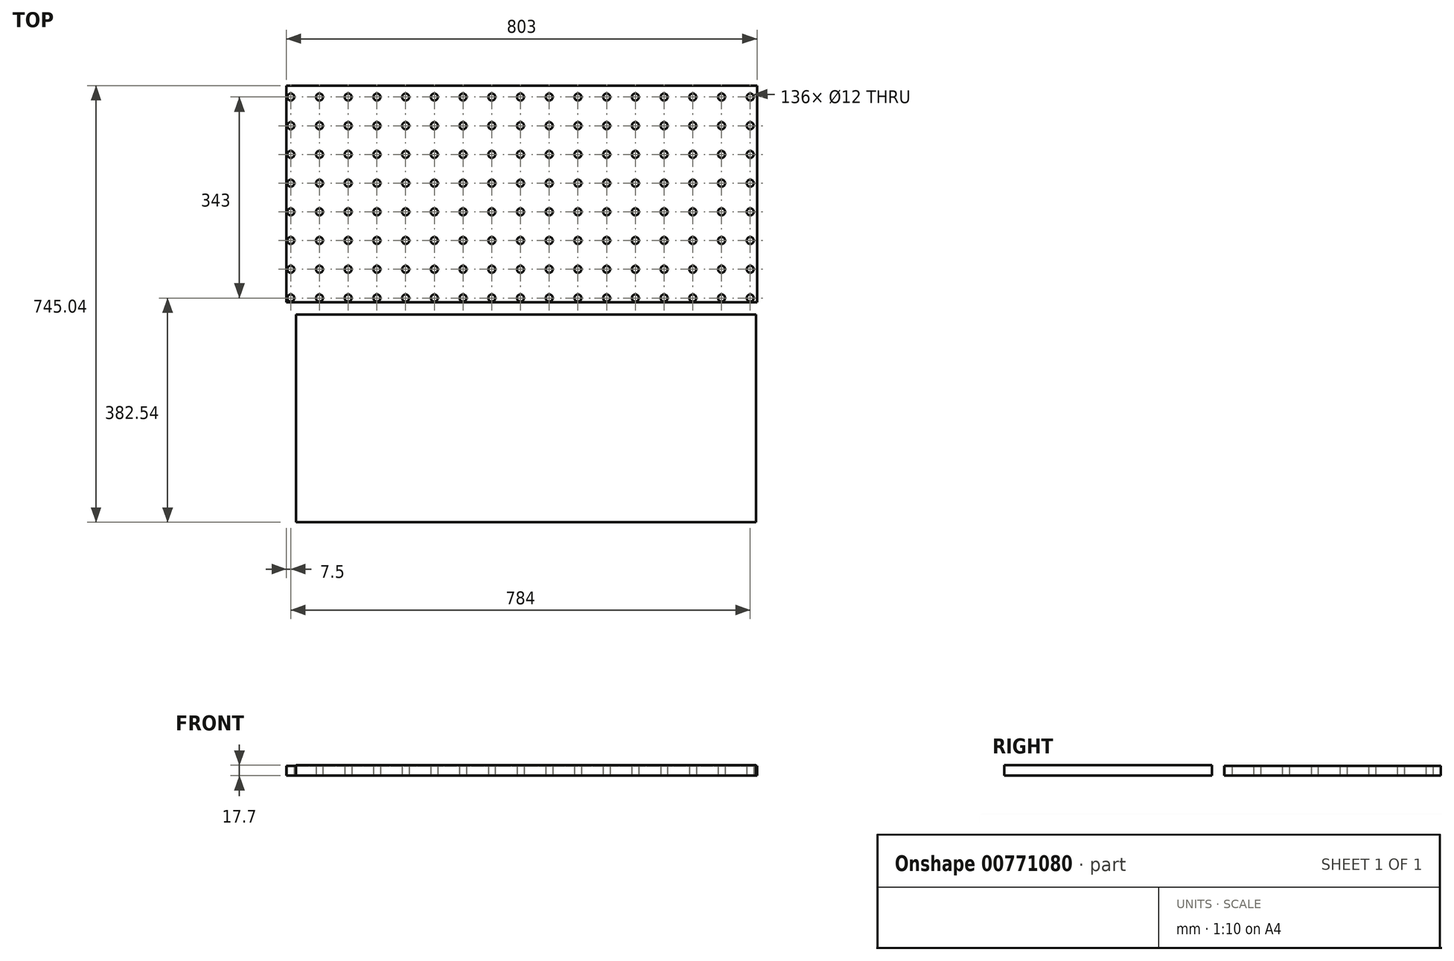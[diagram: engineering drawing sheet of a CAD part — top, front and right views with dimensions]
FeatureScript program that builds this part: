
annotation { "Feature Type Name" : "Feature", "Feature Type Description" : "" }
export const myFeature = defineFeature(function(context is Context, id is Id, definition is map)
    precondition{}
    {
        {
            var Q0;
            Q0=qCreatedBy(makeId("Top.planeOp"),FACE);
            var sketch = newSketch(context, id + "F0", { "sketchPlane" : qUnion([Q0])});
            skLineSegment(sketch, "E0.bottom", {"start": v(-401.5, 185) * mm, "end": v(401.5, 185) * mm});
            skLineSegment(sketch, "E0.top", {"start": v(-401.5, -185) * mm, "end": v(401.5, -185) * mm});
            skLineSegment(sketch, "E0.left", {"start": v(-401.5, 185) * mm, "end": v(-401.5, -185) * mm});
            skLineSegment(sketch, "E0.right", {"start": v(401.5, 185) * mm, "end": v(401.5, -185) * mm});
            skCircle(sketch, "E1", {"center": v(-394, -177.5) * mm, "radius": 6 * mm});
            skCircle(sketch, "E2.0.1.0", {"center": v(-394, -128.5) * mm, "radius": 6 * mm});
            skCircle(sketch, "E2.0.2.0", {"center": v(-394, -79.5) * mm, "radius": 6 * mm});
            skCircle(sketch, "E2.0.3.0", {"center": v(-394, -30.5) * mm, "radius": 6 * mm});
            skCircle(sketch, "E2.0.4.0", {"center": v(-394, 18.5) * mm, "radius": 6 * mm});
            skCircle(sketch, "E2.0.5.0", {"center": v(-394, 67.5) * mm, "radius": 6 * mm});
            skCircle(sketch, "E2.0.6.0", {"center": v(-394, 116.5) * mm, "radius": 6 * mm});
            skCircle(sketch, "E2.0.7.0", {"center": v(-394, 165.5) * mm, "radius": 6 * mm});
            skCircle(sketch, "E2.1.0.0", {"center": v(-345, -177.5) * mm, "radius": 6 * mm});
            skCircle(sketch, "E2.1.1.0", {"center": v(-345, -128.5) * mm, "radius": 6 * mm});
            skCircle(sketch, "E2.1.2.0", {"center": v(-345, -79.5) * mm, "radius": 6 * mm});
            skCircle(sketch, "E2.1.3.0", {"center": v(-345, -30.5) * mm, "radius": 6 * mm});
            skCircle(sketch, "E2.1.4.0", {"center": v(-345, 18.5) * mm, "radius": 6 * mm});
            skCircle(sketch, "E2.1.5.0", {"center": v(-345, 67.5) * mm, "radius": 6 * mm});
            skCircle(sketch, "E2.1.6.0", {"center": v(-345, 116.5) * mm, "radius": 6 * mm});
            skCircle(sketch, "E2.1.7.0", {"center": v(-345, 165.5) * mm, "radius": 6 * mm});
            skCircle(sketch, "E2.2.0.0", {"center": v(-296, -177.5) * mm, "radius": 6 * mm});
            skCircle(sketch, "E2.2.1.0", {"center": v(-296, -128.5) * mm, "radius": 6 * mm});
            skCircle(sketch, "E2.2.2.0", {"center": v(-296, -79.5) * mm, "radius": 6 * mm});
            skCircle(sketch, "E2.2.3.0", {"center": v(-296, -30.5) * mm, "radius": 6 * mm});
            skCircle(sketch, "E2.2.4.0", {"center": v(-296, 18.5) * mm, "radius": 6 * mm});
            skCircle(sketch, "E2.2.5.0", {"center": v(-296, 67.5) * mm, "radius": 6 * mm});
            skCircle(sketch, "E2.2.6.0", {"center": v(-296, 116.5) * mm, "radius": 6 * mm});
            skCircle(sketch, "E2.2.7.0", {"center": v(-296, 165.5) * mm, "radius": 6 * mm});
            skCircle(sketch, "E2.3.0.0", {"center": v(-247, -177.5) * mm, "radius": 6 * mm});
            skCircle(sketch, "E2.3.1.0", {"center": v(-247, -128.5) * mm, "radius": 6 * mm});
            skCircle(sketch, "E2.3.2.0", {"center": v(-247, -79.5) * mm, "radius": 6 * mm});
            skCircle(sketch, "E2.3.3.0", {"center": v(-247, -30.5) * mm, "radius": 6 * mm});
            skCircle(sketch, "E2.3.4.0", {"center": v(-247, 18.5) * mm, "radius": 6 * mm});
            skCircle(sketch, "E2.3.5.0", {"center": v(-247, 67.5) * mm, "radius": 6 * mm});
            skCircle(sketch, "E2.3.6.0", {"center": v(-247, 116.5) * mm, "radius": 6 * mm});
            skCircle(sketch, "E2.3.7.0", {"center": v(-247, 165.5) * mm, "radius": 6 * mm});
            skCircle(sketch, "E2.4.0.0", {"center": v(-198, -177.5) * mm, "radius": 6 * mm});
            skCircle(sketch, "E2.4.1.0", {"center": v(-198, -128.5) * mm, "radius": 6 * mm});
            skCircle(sketch, "E2.4.2.0", {"center": v(-198, -79.5) * mm, "radius": 6 * mm});
            skCircle(sketch, "E2.4.3.0", {"center": v(-198, -30.5) * mm, "radius": 6 * mm});
            skCircle(sketch, "E2.4.4.0", {"center": v(-198, 18.5) * mm, "radius": 6 * mm});
            skCircle(sketch, "E2.4.5.0", {"center": v(-198, 67.5) * mm, "radius": 6 * mm});
            skCircle(sketch, "E2.4.6.0", {"center": v(-198, 116.5) * mm, "radius": 6 * mm});
            skCircle(sketch, "E2.4.7.0", {"center": v(-198, 165.5) * mm, "radius": 6 * mm});
            skCircle(sketch, "E2.5.0.0", {"center": v(-149, -177.5) * mm, "radius": 6 * mm});
            skCircle(sketch, "E2.5.1.0", {"center": v(-149, -128.5) * mm, "radius": 6 * mm});
            skCircle(sketch, "E2.5.2.0", {"center": v(-149, -79.5) * mm, "radius": 6 * mm});
            skCircle(sketch, "E2.5.3.0", {"center": v(-149, -30.5) * mm, "radius": 6 * mm});
            skCircle(sketch, "E2.5.4.0", {"center": v(-149, 18.5) * mm, "radius": 6 * mm});
            skCircle(sketch, "E2.5.5.0", {"center": v(-149, 67.5) * mm, "radius": 6 * mm});
            skCircle(sketch, "E2.5.6.0", {"center": v(-149, 116.5) * mm, "radius": 6 * mm});
            skCircle(sketch, "E2.5.7.0", {"center": v(-149, 165.5) * mm, "radius": 6 * mm});
            skCircle(sketch, "E2.6.0.0", {"center": v(-100, -177.5) * mm, "radius": 6 * mm});
            skCircle(sketch, "E2.6.1.0", {"center": v(-100, -128.5) * mm, "radius": 6 * mm});
            skCircle(sketch, "E2.6.2.0", {"center": v(-100, -79.5) * mm, "radius": 6 * mm});
            skCircle(sketch, "E2.6.3.0", {"center": v(-100, -30.5) * mm, "radius": 6 * mm});
            skCircle(sketch, "E2.6.4.0", {"center": v(-100, 18.5) * mm, "radius": 6 * mm});
            skCircle(sketch, "E2.6.5.0", {"center": v(-100, 67.5) * mm, "radius": 6 * mm});
            skCircle(sketch, "E2.6.6.0", {"center": v(-100, 116.5) * mm, "radius": 6 * mm});
            skCircle(sketch, "E2.6.7.0", {"center": v(-100, 165.5) * mm, "radius": 6 * mm});
            skCircle(sketch, "E2.7.0.0", {"center": v(-51, -177.5) * mm, "radius": 6 * mm});
            skCircle(sketch, "E2.7.1.0", {"center": v(-51, -128.5) * mm, "radius": 6 * mm});
            skCircle(sketch, "E2.7.2.0", {"center": v(-51, -79.5) * mm, "radius": 6 * mm});
            skCircle(sketch, "E2.7.3.0", {"center": v(-51, -30.5) * mm, "radius": 6 * mm});
            skCircle(sketch, "E2.7.4.0", {"center": v(-51, 18.5) * mm, "radius": 6 * mm});
            skCircle(sketch, "E2.7.5.0", {"center": v(-51, 67.5) * mm, "radius": 6 * mm});
            skCircle(sketch, "E2.7.6.0", {"center": v(-51, 116.5) * mm, "radius": 6 * mm});
            skCircle(sketch, "E2.7.7.0", {"center": v(-51, 165.5) * mm, "radius": 6 * mm});
            skCircle(sketch, "E2.8.0.0", {"center": v(-2, -177.5) * mm, "radius": 6 * mm});
            skCircle(sketch, "E2.8.1.0", {"center": v(-2, -128.5) * mm, "radius": 6 * mm});
            skCircle(sketch, "E2.8.2.0", {"center": v(-2, -79.5) * mm, "radius": 6 * mm});
            skCircle(sketch, "E2.8.3.0", {"center": v(-2, -30.5) * mm, "radius": 6 * mm});
            skCircle(sketch, "E2.8.4.0", {"center": v(-2, 18.5) * mm, "radius": 6 * mm});
            skCircle(sketch, "E2.8.5.0", {"center": v(-2, 67.5) * mm, "radius": 6 * mm});
            skCircle(sketch, "E2.8.6.0", {"center": v(-2, 116.5) * mm, "radius": 6 * mm});
            skCircle(sketch, "E2.8.7.0", {"center": v(-2, 165.5) * mm, "radius": 6 * mm});
            skCircle(sketch, "E2.9.0.0", {"center": v(47, -177.5) * mm, "radius": 6 * mm});
            skCircle(sketch, "E2.9.1.0", {"center": v(47, -128.5) * mm, "radius": 6 * mm});
            skCircle(sketch, "E2.9.2.0", {"center": v(47, -79.5) * mm, "radius": 6 * mm});
            skCircle(sketch, "E2.9.3.0", {"center": v(47, -30.5) * mm, "radius": 6 * mm});
            skCircle(sketch, "E2.9.4.0", {"center": v(47, 18.5) * mm, "radius": 6 * mm});
            skCircle(sketch, "E2.9.5.0", {"center": v(47, 67.5) * mm, "radius": 6 * mm});
            skCircle(sketch, "E2.9.6.0", {"center": v(47, 116.5) * mm, "radius": 6 * mm});
            skCircle(sketch, "E2.9.7.0", {"center": v(47, 165.5) * mm, "radius": 6 * mm});
            skCircle(sketch, "E2.10.0.0", {"center": v(96, -177.5) * mm, "radius": 6 * mm});
            skCircle(sketch, "E2.10.1.0", {"center": v(96, -128.5) * mm, "radius": 6 * mm});
            skCircle(sketch, "E2.10.2.0", {"center": v(96, -79.5) * mm, "radius": 6 * mm});
            skCircle(sketch, "E2.10.3.0", {"center": v(96, -30.5) * mm, "radius": 6 * mm});
            skCircle(sketch, "E2.10.4.0", {"center": v(96, 18.5) * mm, "radius": 6 * mm});
            skCircle(sketch, "E2.10.5.0", {"center": v(96, 67.5) * mm, "radius": 6 * mm});
            skCircle(sketch, "E2.10.6.0", {"center": v(96, 116.5) * mm, "radius": 6 * mm});
            skCircle(sketch, "E2.10.7.0", {"center": v(96, 165.5) * mm, "radius": 6 * mm});
            skCircle(sketch, "E2.11.0.0", {"center": v(145, -177.5) * mm, "radius": 6 * mm});
            skCircle(sketch, "E2.11.1.0", {"center": v(145, -128.5) * mm, "radius": 6 * mm});
            skCircle(sketch, "E2.11.2.0", {"center": v(145, -79.5) * mm, "radius": 6 * mm});
            skCircle(sketch, "E2.11.3.0", {"center": v(145, -30.5) * mm, "radius": 6 * mm});
            skCircle(sketch, "E2.11.4.0", {"center": v(145, 18.5) * mm, "radius": 6 * mm});
            skCircle(sketch, "E2.11.5.0", {"center": v(145, 67.5) * mm, "radius": 6 * mm});
            skCircle(sketch, "E2.11.6.0", {"center": v(145, 116.5) * mm, "radius": 6 * mm});
            skCircle(sketch, "E2.11.7.0", {"center": v(145, 165.5) * mm, "radius": 6 * mm});
            skCircle(sketch, "E2.12.0.0", {"center": v(194, -177.5) * mm, "radius": 6 * mm});
            skCircle(sketch, "E2.12.1.0", {"center": v(194, -128.5) * mm, "radius": 6 * mm});
            skCircle(sketch, "E2.12.2.0", {"center": v(194, -79.5) * mm, "radius": 6 * mm});
            skCircle(sketch, "E2.12.3.0", {"center": v(194, -30.5) * mm, "radius": 6 * mm});
            skCircle(sketch, "E2.12.4.0", {"center": v(194, 18.5) * mm, "radius": 6 * mm});
            skCircle(sketch, "E2.12.5.0", {"center": v(194, 67.5) * mm, "radius": 6 * mm});
            skCircle(sketch, "E2.12.6.0", {"center": v(194, 116.5) * mm, "radius": 6 * mm});
            skCircle(sketch, "E2.12.7.0", {"center": v(194, 165.5) * mm, "radius": 6 * mm});
            skCircle(sketch, "E2.13.0.0", {"center": v(243, -177.5) * mm, "radius": 6 * mm});
            skCircle(sketch, "E2.13.1.0", {"center": v(243, -128.5) * mm, "radius": 6 * mm});
            skCircle(sketch, "E2.13.2.0", {"center": v(243, -79.5) * mm, "radius": 6 * mm});
            skCircle(sketch, "E2.13.3.0", {"center": v(243, -30.5) * mm, "radius": 6 * mm});
            skCircle(sketch, "E2.13.4.0", {"center": v(243, 18.5) * mm, "radius": 6 * mm});
            skCircle(sketch, "E2.13.5.0", {"center": v(243, 67.5) * mm, "radius": 6 * mm});
            skCircle(sketch, "E2.13.6.0", {"center": v(243, 116.5) * mm, "radius": 6 * mm});
            skCircle(sketch, "E2.13.7.0", {"center": v(243, 165.5) * mm, "radius": 6 * mm});
            skCircle(sketch, "E2.14.0.0", {"center": v(292, -177.5) * mm, "radius": 6 * mm});
            skCircle(sketch, "E2.14.1.0", {"center": v(292, -128.5) * mm, "radius": 6 * mm});
            skCircle(sketch, "E2.14.2.0", {"center": v(292, -79.5) * mm, "radius": 6 * mm});
            skCircle(sketch, "E2.14.3.0", {"center": v(292, -30.5) * mm, "radius": 6 * mm});
            skCircle(sketch, "E2.14.4.0", {"center": v(292, 18.5) * mm, "radius": 6 * mm});
            skCircle(sketch, "E2.14.5.0", {"center": v(292, 67.5) * mm, "radius": 6 * mm});
            skCircle(sketch, "E2.14.6.0", {"center": v(292, 116.5) * mm, "radius": 6 * mm});
            skCircle(sketch, "E2.14.7.0", {"center": v(292, 165.5) * mm, "radius": 6 * mm});
            skCircle(sketch, "E2.15.0.0", {"center": v(341, -177.5) * mm, "radius": 6 * mm});
            skCircle(sketch, "E2.15.1.0", {"center": v(341, -128.5) * mm, "radius": 6 * mm});
            skCircle(sketch, "E2.15.2.0", {"center": v(341, -79.5) * mm, "radius": 6 * mm});
            skCircle(sketch, "E2.15.3.0", {"center": v(341, -30.5) * mm, "radius": 6 * mm});
            skCircle(sketch, "E2.15.4.0", {"center": v(341, 18.5) * mm, "radius": 6 * mm});
            skCircle(sketch, "E2.15.5.0", {"center": v(341, 67.5) * mm, "radius": 6 * mm});
            skCircle(sketch, "E2.15.6.0", {"center": v(341, 116.5) * mm, "radius": 6 * mm});
            skCircle(sketch, "E2.15.7.0", {"center": v(341, 165.5) * mm, "radius": 6 * mm});
            skCircle(sketch, "E2.16.0.0", {"center": v(390, -177.5) * mm, "radius": 6 * mm});
            skCircle(sketch, "E2.16.1.0", {"center": v(390, -128.5) * mm, "radius": 6 * mm});
            skCircle(sketch, "E2.16.2.0", {"center": v(390, -79.5) * mm, "radius": 6 * mm});
            skCircle(sketch, "E2.16.3.0", {"center": v(390, -30.5) * mm, "radius": 6 * mm});
            skCircle(sketch, "E2.16.4.0", {"center": v(390, 18.5) * mm, "radius": 6 * mm});
            skCircle(sketch, "E2.16.5.0", {"center": v(390, 67.5) * mm, "radius": 6 * mm});
            skCircle(sketch, "E2.16.6.0", {"center": v(390, 116.5) * mm, "radius": 6 * mm});
            skCircle(sketch, "E2.16.7.0", {"center": v(390, 165.5) * mm, "radius": 6 * mm});
            skLineSegment(sketch, "E2.direction1", {"start": v(-394, -177.5) * mm, "end": v(-345, -177.5) * mm, "construction": true});
            skLineSegment(sketch, "E2.direction2", {"start": v(-394, -177.5) * mm, "end": v(-394, -128.5) * mm, "construction": true});
            skSolve(sketch);
        }
        {
            var Q0;
            Q0 = qSketchRegion(id + "F0", true);
            extrude(context, id + "F1", {"entities" : qUnion([Q0]), "depth" : 16.7 * mm, "offsetDistance" : 25 * mm});
        }
        {
            var Q0;
            Q0=qCreatedBy(makeId("Top.planeOp"),FACE);
            var sketch = newSketch(context, id + "F2", { "sketchPlane" : qUnion([Q0])});
            skLineSegment(sketch, "E3.bottom", {"start": v(-384.97, -206.04) * mm, "end": v(400.03, -206.04) * mm});
            skLineSegment(sketch, "E3.top", {"start": v(-384.97, -560.04) * mm, "end": v(400.03, -560.04) * mm});
            skLineSegment(sketch, "E3.left", {"start": v(-384.97, -206.04) * mm, "end": v(-384.97, -560.04) * mm});
            skLineSegment(sketch, "E3.right", {"start": v(400.03, -206.04) * mm, "end": v(400.03, -560.04) * mm});
            skLineSegment(sketch, "E4.0", {"start": v(-401.5, -185) * mm, "end": v(401.5, -185) * mm, "construction": true});
            skSolve(sketch);
        }
        {
            var Q0;
            Q0 = qSketchRegion(id + "F2", true);
            extrude(context, id + "F3", {"entities" : qUnion([Q0]), "depth" : 17.7 * mm, "offsetDistance" : 25 * mm});
        }
    });
